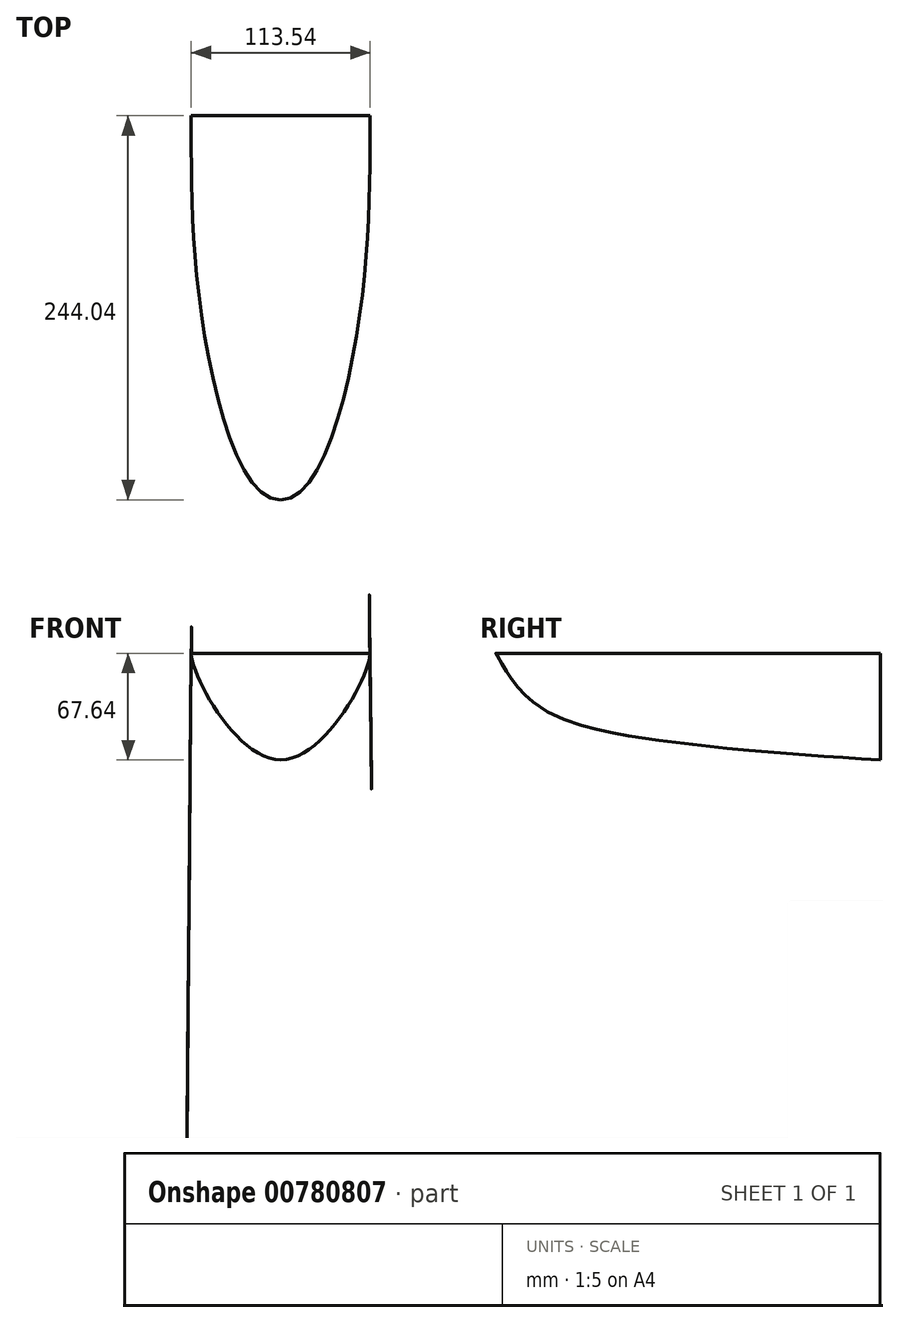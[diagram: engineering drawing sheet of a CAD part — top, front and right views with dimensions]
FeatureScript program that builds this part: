
annotation { "Feature Type Name" : "Feature", "Feature Type Description" : "" }
export const myFeature = defineFeature(function(context is Context, id is Id, definition is map)
    precondition{}
    {
        {
            var Q0;
            Q0=qCreatedBy(makeId("Front.planeOp"),FACE);
            var sketch = newSketch(context, id + "F0", { "sketchPlane" : qUnion([Q0])});
            skLineSegment(sketch, "E0.bottom", {"start": v(-56.77, -13.3) * mm, "end": v(56.77, -13.3) * mm, "construction": true});
            skLineSegment(sketch, "E0.top", {"start": v(-56.77, 0) * mm, "end": v(56.77, 0) * mm});
            skLineSegment(sketch, "E0.left", {"start": v(-56.77, 0) * mm, "end": v(-56.77, -13.3) * mm, "construction": true});
            skLineSegment(sketch, "E0.right", {"start": v(56.77, 0) * mm, "end": v(56.77, -13.3) * mm, "construction": true});
            skLineSegment(sketch, "E1", {"start": v(0, 0) * mm, "end": v(0, -67.64) * mm, "construction": true});
            skFitSpline(sketch, "E2", {"points": [v(-56.77, 0) * mm, v(0, -67.64) * mm, v(56.77, 0) * mm], "startDerivative": vector(0, -79.85) * mm, "endDerivative": vector(0, 79.85) * mm});
            skSolve(sketch);
        }
        {
            var Q0;
            Q0=qCreatedBy(makeId("Top.planeOp"),FACE);
            var sketch = newSketch(context, id + "F1", { "sketchPlane" : qUnion([Q0])});
            skLineSegment(sketch, "E3", {"start": v(0, 0) * mm, "end": v(0, -244.04) * mm});
            skSolve(sketch);
        }
        {
            var Q0;
            Q0=qCreatedBy(makeId("Right.planeOp"),FACE);
            var sketch = newSketch(context, id + "F2", { "sketchPlane" : qUnion([Q0])});
            skFitSpline(sketch, "E4", {"points": [v(-244.04, 0) * mm, v(-176.4, -49.08) * mm, v(0, -67.64) * mm], "startDerivative": vector(117.33, -222.79) * mm, "endDerivative": vector(121.04, -7.6) * mm});
            skSolve(sketch);
        }
        {
            var Q0;
            Q0=qCreatedBy(makeId("Top.planeOp"),FACE);
            var sketch = newSketch(context, id + "F3", { "sketchPlane" : qUnion([Q0])});
            skFitSpline(sketch, "E5", {"points": [v(-56.77, 0) * mm, v(-47.8, -142.17) * mm, v(0, -244.04) * mm], "startDerivative": vector(0, -238.17) * mm, "endDerivative": vector(152.31, 0) * mm});
            skFitSpline(sketch, "E6.MirrorCS", {"points": [v(56.77, 0) * mm, v(47.8, -142.17) * mm, v(0, -244.04) * mm], "startDerivative": vector(0, -238.17) * mm, "endDerivative": vector(-152.31, 0) * mm});
            skSolve(sketch);
        }
        {
            var Q0;
            Q0=makeQuery(id+"F0.imprint","IMPRINT",FACE,{"disambiguationData":[TD([[makeQuery(id+"F0.imprint","IMPRINT",EDGE,{"derivedFrom":sQuery(id+"F0.wireOp",EDGE,"E0.top")}),-1.0]])]});
            var Q1;
            Q1=sQuery(id+"F1.wireOp",VERTEX,"E3.end");
            var Q2;
            Q2=sQuery(id+"F0.wireOp",EDGE,"E2");
            var Q3;
            Q3=sQuery(id+"F1.wireOp",VERTEX,"E3.end");
            var Q4;
            Q4=sQuery(id+"F2.wireOp",EDGE,"E4");
            var Q5;
            Q5=sQuery(id+"F3.wireOp",EDGE,"E5");
            var Q6;
            Q6=sQuery(id+"F3.wireOp",EDGE,"E6.MirrorCS");
            loft(context, id + "F4", {"addGuides" : true, "sheetProfilesArray" : [{ "sheetProfileEntities" : qUnion([Q0]) }, { "sheetProfileEntities" : qUnion([Q1]) }], "wireProfilesArray" : [{ "wireProfileEntities" : qUnion([Q2]) }, { "wireProfileEntities" : qUnion([Q3]) }], "guidesArray" : [{ "guideEntities" : qUnion([Q4]), "guideDerivativeType" : LoftGuideDerivativeType.DEFAULT, "guideDerivativeMagnitude" : 1 }, { "guideEntities" : qUnion([Q5]), "guideDerivativeType" : LoftGuideDerivativeType.DEFAULT, "guideDerivativeMagnitude" : 1 }, { "guideEntities" : qUnion([Q6]), "guideDerivativeType" : LoftGuideDerivativeType.DEFAULT, "guideDerivativeMagnitude" : 1 }]});
        }
    });
